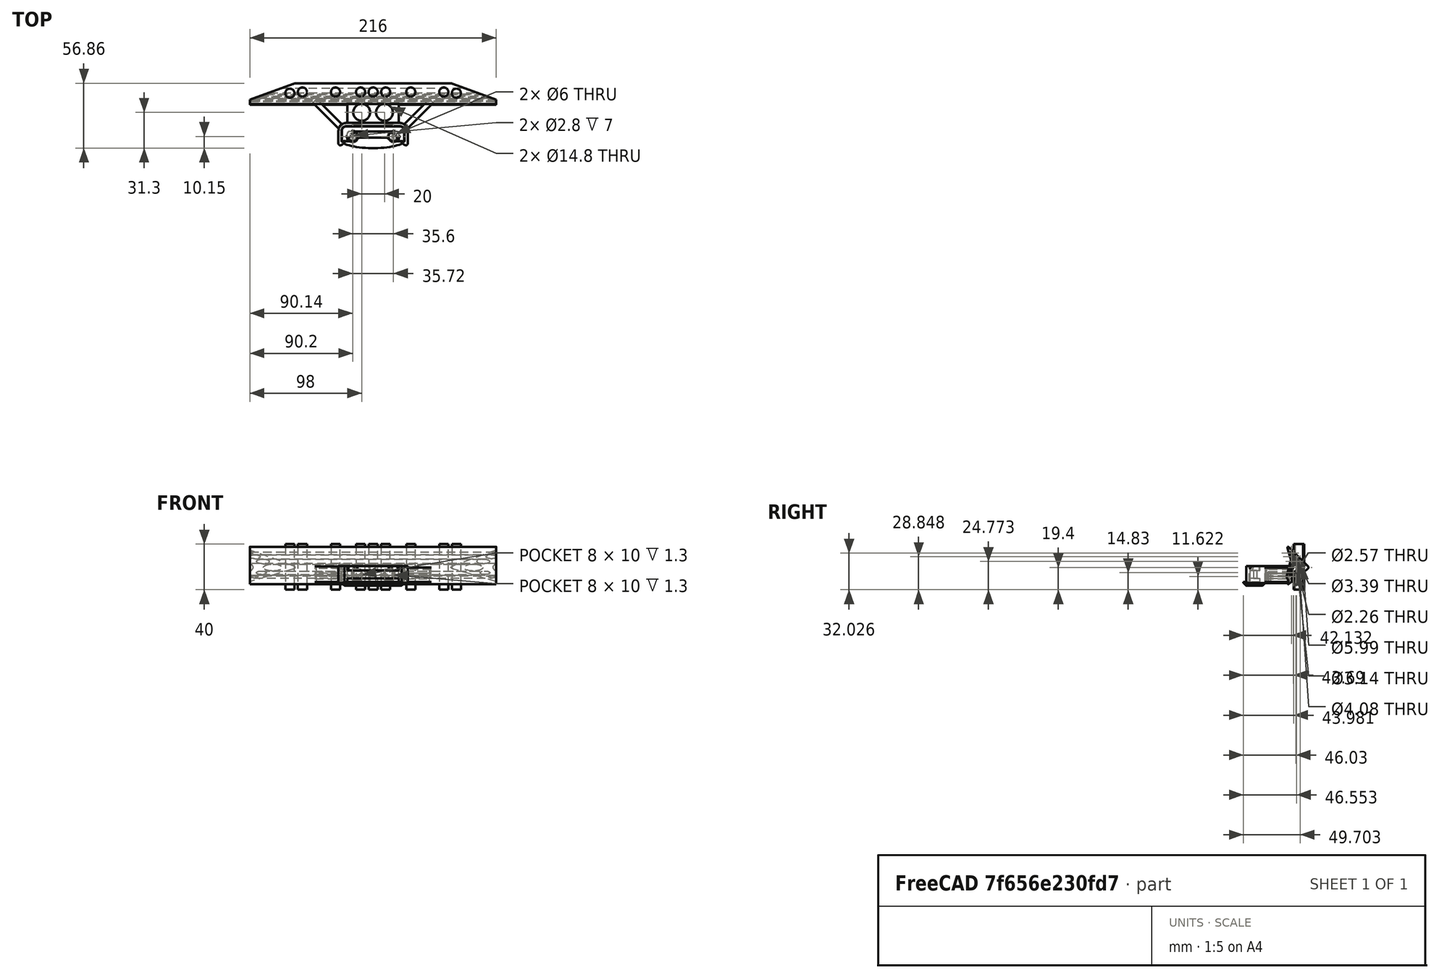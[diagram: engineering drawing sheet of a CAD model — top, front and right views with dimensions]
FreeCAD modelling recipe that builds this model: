
FCSTD DOCUMENT  (FreeCAD 0.21R0.20.1)
Label: 058
License: All rights reserved
LicenseURL: http://en.wikipedia.org/wiki/All_rights_reserved
objects: Part::Cylinder×29, Part::MultiFuse×13, Sketcher::SketchObject×7, Part::Extrusion×7, Part::Box×7, Part::Cut×6, Part::Fillet×5, Part::Chamfer×2
note: 76 computed .brp shape members not serialized (recipe doc carries the construction recipe); baked Part::Feature solids carry a one-line shape summary decoded from their .brp

FEATURE [Sketcher::SketchObject] Sketch  label="attatchmentPiece"
  FullyConstrained = true
  sketch-geometry (20):
    g0: LineSegment StartX=21.05 StartY=0 StartZ=0 EndX=21.05 EndY=-1 EndZ=0
    g1: LineSegment StartX=21.05 StartY=-1 StartZ=0 EndX=21.05 EndY=-4.3 EndZ=0
    g2: LineSegment StartX=-24.15 StartY=4.3 StartZ=0 EndX=21.05 EndY=4.3 EndZ=0
    g3: LineSegment StartX=21.05 StartY=0 StartZ=0 EndX=21.05 EndY=4.3 EndZ=0
    g4-g7: Circle x4 (B-spline internal-alignment scaffolding for g8; pole/knot coordinates omitted)
    g8: BSplineCurve PolesCount=4 KnotsCount=2 Degree=3 IsPeriodic=0
    g9: GeomPoint X=10.05 Y=-1 Z=0
    g10: GeomPoint X=14.55 Y=-4.3 Z=0
    g11: LineSegment StartX=10.05 StartY=-1 StartZ=0 EndX=-10.05 EndY=-1 EndZ=0
    g12: LineSegment StartX=14.55 StartY=-4.3 StartZ=0 EndX=21.05 EndY=-4.3 EndZ=0
    g13: LineSegment StartX=-24.15 StartY=4.3 StartZ=0 EndX=-24.15 EndY=-4.3 EndZ=0
    g14: LineSegment StartX=-13.15 StartY=-1 StartZ=0 EndX=-10.05 EndY=-1 EndZ=0
    g15: LineSegment StartX=-24.15 StartY=-4.3 StartZ=0 EndX=-19.35 EndY=-4.3 EndZ=0
    g16: LineSegment StartX=-19.35 StartY=-4.3 StartZ=0 EndX=-17.65 EndY=-4.3 EndZ=0
    g17: BSplineCurve PolesCount=4 KnotsCount=2 Degree=3 IsPeriodic=0
    g18: Circle CenterX=16.25 CenterY=0 CenterZ=0 NormalX=0 NormalY=0 NormalZ=1 AngleXU=0 Radius=1.4
    g19: Circle CenterX=-19.35 CenterY=0 CenterZ=0 NormalX=0 NormalY=0 NormalZ=1 AngleXU=0 Radius=1.4
  constraints (41):
    c: Vertical(g0)
    c: Coincident(g1,g0)
    c: Vertical(g1)
    c: Block(g0)
    c: Horizontal(g2)
    c: Vertical(g3)
    c: Coincident(g3,g2)
    c: Block(g2)
    c: Block(g3)
    c: Weight(g4) = 1
    c: Equal(g4,g5)
    c: Equal(g4,g6)
    c: Equal(g4,g7)
    c: InternalAlignment(g4-g7 -> g8) x4
    c: InternalAlignment(g9,g8)
    c: InternalAlignment(g10,g8)
    c: Block(g8)
    c: Coincident(g11,g8)
    c: Horizontal(g11)
    c: Coincident(g12,g8)
    c: Coincident(g12,g1)
    c: Horizontal(g12)
    c: Distance(g2) = 45.2
    c: Coincident(g13,g2)
    c: Vertical(g13)
    c: Horizontal(g14)
    c: Distance(g14) = 3.1
    c: Horizontal(g15)
    c: Block(g17)
    c: Coincident(g16,g15)
    c: Coincident(g16,g17)
    c: Horizontal(g16)
    c: Block(g16)
    c: Coincident(g17,g14)
    c: Block(g15)
    c: Block(g11)
    c: Block(g13)
    c: Distance(g15) = 4.8
    c: Distance(g16) = 1.7
    c: Block(g18)
    c: Block(g19)
FEATURE [Part::Extrusion] Extrude  label="attatchmentPiece001"
  Base = -> Sketch
  Dir = (0,0,1)
  DirMode = 2
  FaceMakerClass = Part::FaceMakerBullseye
  LengthFwd = 7
  LengthRev = 0
  Solid = true
  Symmetric = false
FEATURE [Sketcher::SketchObject] Sketch001  label="attatchmentPieceSurround"
  FullyConstrained = true
  sketch-geometry (18):
    g0: LineSegment StartX=25.85 StartY=-4.3 StartZ=0 EndX=21.05 EndY=-4.3 EndZ=0
    g1: LineSegment StartX=25.85 StartY=-4.3 StartZ=0 EndX=25.85 EndY=4.3 EndZ=0
    g2: LineSegment StartX=-21.05 StartY=8.9 StartZ=0 EndX=21.05 EndY=8.9 EndZ=0
    g3: Circle CenterX=21.05 CenterY=8.9 CenterZ=0 NormalX=0 NormalY=0 NormalZ=1 AngleXU=0 Radius=1
    g4: Circle CenterX=25.85 CenterY=8.9 CenterZ=0 NormalX=0 NormalY=0 NormalZ=1 AngleXU=0 Radius=1
    g5: Circle CenterX=25.85 CenterY=4.3 CenterZ=0 NormalX=0 NormalY=0 NormalZ=1 AngleXU=0 Radius=1
    g6: BSplineCurve PolesCount=3 KnotsCount=2 Degree=2 IsPeriodic=0
    g7: GeomPoint X=21.05 Y=8.9 Z=0
    g8: GeomPoint X=25.85 Y=4.3 Z=0
    g9: ArcOfCircle CenterX=19.45 CenterY=2.7 CenterZ=0 NormalX=0 NormalY=0 NormalZ=1 AngleXU=0 Radius=1.6 StartAngle=0 EndAngle=1.5708
    g10: LineSegment StartX=21.05 StartY=2.7 StartZ=0 EndX=21.05 EndY=-4.3 EndZ=0
    g11: BSplineCurve PolesCount=3 KnotsCount=2 Degree=2 IsPeriodic=0
    g12: LineSegment StartX=-28.95 StartY=-4.3 StartZ=0 EndX=-28.95 EndY=4.3 EndZ=0
    g13: LineSegment StartX=-24.15 StartY=-4.3 StartZ=0 EndX=-28.95 EndY=-4.3 EndZ=0
    g14: LineSegment StartX=-24.15 StartY=2.7 StartZ=0 EndX=-24.15 EndY=-4.3 EndZ=0
    g15: ArcOfCircle CenterX=-22.55 CenterY=2.7 CenterZ=0 NormalX=0 NormalY=0 NormalZ=1 AngleXU=0 Radius=1.6 StartAngle=1.5708 EndAngle=3.14159
    g16: LineSegment StartX=-24.15 StartY=8.9 StartZ=0 EndX=-21.05 EndY=8.9 EndZ=0
    g17: LineSegment StartX=-22.55 StartY=4.3 StartZ=0 EndX=19.45 EndY=4.3 EndZ=0
  constraints (38):
    c: Horizontal(g0)
    c: Vertical(g1)
    c: Coincident(g1,g0)
    c: Horizontal(g2)
    c: Distance(g2) = 42.1
    c: Block(g2)
    c: Coincident(g6,g2)
    c: Weight(g3) = 1
    c: Equal(g3,g4)
    c: Equal(g3,g5)
    c: Coincident(g6,g1)
    c: InternalAlignment(g3,g6)
    c: InternalAlignment(g4,g6)
    c: InternalAlignment(g5,g6)
    c: InternalAlignment(g7,g6)
    c: InternalAlignment(g8,g6)
    c: Block(g0)
    c: Block(g6)
    c: Block(g9)
    c: Coincident(g10,g9)
    c: Coincident(g10,g0)
    c: Vertical(g10)
    c: Horizontal(g13)
    c: Coincident(g12,g13)
    c: Vertical(g12)
    c: Coincident(g11,g12)
    c: Block(g12)
    c: Block(g11)
    c: Block(g15)
    c: Coincident(g14,g15)
    c: Coincident(g14,g13)
    c: Vertical(g14)
    c: Coincident(g16,g11)
    c: Coincident(g16,g2)
    c: Horizontal(g16)
    c: Coincident(g17,g15)
    c: Coincident(g17,g9)
    c: Horizontal(g17)
FEATURE [Part::Extrusion] Extrude001  label="attatchmentPieceSurround001"
  Base = -> Sketch001
  Dir = (0,0,1)
  DirMode = 2
  FaceMakerClass = Part::FaceMakerBullseye
  LengthFwd = 14.7
  LengthRev = 0
  Placement = pos=(0,0,-4.1) rot=(0,0,1;0rad)
  Solid = true
  Symmetric = false
FEATURE [Sketcher::SketchObject] Sketch002  label="attatchmentPieceEndScrewHoleCaps"
  FullyConstrained = true
  sketch-geometry (10):
    g0: ArcOfCircle CenterX=16.25 CenterY=0 CenterZ=0 NormalX=0 NormalY=0 NormalZ=1 AngleXU=0 Radius=4.3 StartAngle=2.05456 EndAngle=5.79942
    g1: LineSegment StartX=14.25 StartY=3.80657 StartZ=0 EndX=14.25 EndY=6 EndZ=0
    g2: LineSegment StartX=20.0566 StartY=-2 StartZ=0 EndX=22.25 EndY=-2 EndZ=0
    g3: LineSegment StartX=22.25 StartY=-2 StartZ=0 EndX=22.25 EndY=6 EndZ=0
    g4: LineSegment StartX=14.25 StartY=6 StartZ=0 EndX=22.25 EndY=6 EndZ=0
    g5: LineSegment StartX=-25.35 StartY=-2 StartZ=0 EndX=-25.35 EndY=6 EndZ=0
    g6: LineSegment StartX=-25.35 StartY=-2 StartZ=0 EndX=-23.1566 EndY=-2 EndZ=0
    g7: LineSegment StartX=-17.35 StartY=6 StartZ=0 EndX=-25.35 EndY=6 EndZ=0
    g8: LineSegment StartX=-17.35 StartY=3.80657 StartZ=0 EndX=-17.35 EndY=6 EndZ=0
    g9: ArcOfCircle CenterX=-19.35 CenterY=0 CenterZ=0 NormalX=0 NormalY=0 NormalZ=1 AngleXU=0 Radius=4.3 StartAngle=3.62536 EndAngle=7.37022
  constraints (25):
    c: Block(g0)
    c: Vertical(g1)
    c: Horizontal(g2)
    c: Coincident(g3,g2)
    c: Vertical(g3)
    c: Coincident(g4,g1)
    c: Horizontal(g4)
    c: Coincident(g3,g4)
    c: Block(g4)
    c: Block(g3)
    c: Coincident(g0,g1)
    c: Coincident(g0,g2)
    c: Block(g1)
    c: Block(g9)
    c: Horizontal(g6)
    c: Vertical(g8)
    c: Coincident(g7,g8)
    c: Horizontal(g7)
    c: Coincident(g5,g6)
    c: Vertical(g5)
    c: Coincident(g5,g7)
    c: Block(g7)
    c: Block(g5)
    c: Coincident(g9,g6)
    c: Coincident(g9,g8)
FEATURE [Part::Extrusion] Extrude002  label="attatchmentPieceEndScrewHoleCaps001"
  Base = -> Sketch002
  Dir = (0,0,1)
  DirMode = 2
  FaceMakerClass = Part::FaceMakerBullseye
  LengthFwd = 3.6
  LengthRev = 0
  Placement = pos=(0,0,7) rot=(0,0,1;0rad)
  Solid = true
  Symmetric = false
FEATURE [Sketcher::SketchObject] Sketch003  label="mainBumpperPieceAttatchment"
  FullyConstrained = true
  sketch-geometry (42):
    g0: Circle CenterX=28.85 CenterY=4.3 CenterZ=0 NormalX=0 NormalY=0 NormalZ=1 AngleXU=0 Radius=1
    g1: Circle CenterX=28.85 CenterY=11.9 CenterZ=0 NormalX=0 NormalY=0 NormalZ=1 AngleXU=0 Radius=1
    g2: Circle CenterX=21.05 CenterY=11.9 CenterZ=0 NormalX=0 NormalY=0 NormalZ=1 AngleXU=0 Radius=1
    g3: BSplineCurve PolesCount=3 KnotsCount=2 Degree=2 IsPeriodic=0
    g4: GeomPoint X=28.85 Y=4.3 Z=0
    g5: GeomPoint X=21.05 Y=11.9 Z=0
    g6: LineSegment StartX=-21.05 StartY=11.9 StartZ=0 EndX=21.05 EndY=11.9 EndZ=0
    g7: LineSegment StartX=28.85 StartY=4.3 StartZ=0 EndX=28.85 EndY=-4.3 EndZ=0
    g8: Circle CenterX=21.05 CenterY=9.2 CenterZ=0 NormalX=0 NormalY=0 NormalZ=1 AngleXU=0 Radius=1
    g9: Circle CenterX=26.15 CenterY=9.2 CenterZ=0 NormalX=0 NormalY=0 NormalZ=1 AngleXU=0 Radius=1
    g10: Circle CenterX=26.15 CenterY=4.3 CenterZ=0 NormalX=0 NormalY=0 NormalZ=1 AngleXU=0 Radius=1
    g11: BSplineCurve PolesCount=3 KnotsCount=2 Degree=2 IsPeriodic=0
    g12: GeomPoint X=21.05 Y=9.2 Z=0
    g13: GeomPoint X=26.15 Y=4.3 Z=0
    g14: LineSegment StartX=-21.05 StartY=9.2 StartZ=0 EndX=21.05 EndY=9.2 EndZ=0
    g15: LineSegment StartX=26.15 StartY=-4.3 StartZ=0 EndX=26.15 EndY=4.3 EndZ=0
    g16: LineSegment StartX=26.15 StartY=-4.3 StartZ=0 EndX=26.15 EndY=-4.6 EndZ=0
    g17: LineSegment StartX=23.45 StartY=-4.6 StartZ=0 EndX=26.15 EndY=-4.6 EndZ=0
    g18: LineSegment StartX=28.85 StartY=-4.3 StartZ=0 EndX=28.85 EndY=-7.9 EndZ=0
    g19: LineSegment StartX=23.45 StartY=-4.6 StartZ=0 EndX=23.45 EndY=-5.3 EndZ=0
    g20: Circle CenterX=28.85 CenterY=-7.9 CenterZ=0 NormalX=0 NormalY=0 NormalZ=1 AngleXU=0 Radius=1
    g21: Circle CenterX=26.15 CenterY=-8.2 CenterZ=0 NormalX=0 NormalY=0 NormalZ=1 AngleXU=0 Radius=1
    g22: Circle CenterX=23.45 CenterY=-5.3 CenterZ=0 NormalX=0 NormalY=0 NormalZ=1 AngleXU=0 Radius=1
    g23: BSplineCurve PolesCount=3 KnotsCount=2 Degree=2 IsPeriodic=0
    g24: GeomPoint X=28.85 Y=-7.9 Z=0
    g25: GeomPoint X=23.45 Y=-5.3 Z=0
    g26: LineSegment StartX=-21.05 StartY=9.2 StartZ=0 EndX=-24.15 EndY=9.2 EndZ=0
    g27: BSplineCurve PolesCount=3 KnotsCount=2 Degree=2 IsPeriodic=0
    g28: LineSegment StartX=-29.25 StartY=-4.3 StartZ=0 EndX=-29.25 EndY=-4.6 EndZ=0
    g29: LineSegment StartX=-29.25 StartY=-4.6 StartZ=0 EndX=-26.55 EndY=-4.6 EndZ=0
    g30: LineSegment StartX=-31.95 StartY=-4.3 StartZ=0 EndX=-31.95 EndY=-7.9 EndZ=0
    g31: LineSegment StartX=-26.55 StartY=-4.6 StartZ=0 EndX=-26.55 EndY=-5.3 EndZ=0
    g32: Circle CenterX=-31.95 CenterY=-7.9 CenterZ=0 NormalX=0 NormalY=0 NormalZ=1 AngleXU=0 Radius=1
    g33: Circle CenterX=-29.25 CenterY=-8.2 CenterZ=0 NormalX=0 NormalY=0 NormalZ=1 AngleXU=0 Radius=1
    g34: Circle CenterX=-26.55 CenterY=-5.3 CenterZ=0 NormalX=0 NormalY=0 NormalZ=1 AngleXU=0 Radius=1
    g35: BSplineCurve PolesCount=3 KnotsCount=2 Degree=2 IsPeriodic=0
    g36: GeomPoint X=-31.95 Y=-7.9 Z=0
    g37: GeomPoint X=-26.55 Y=-5.3 Z=0
    g38: LineSegment StartX=-31.95 StartY=4.3 StartZ=0 EndX=-31.95 EndY=-4.3 EndZ=0
    g39: LineSegment StartX=-29.25 StartY=-4.3 StartZ=0 EndX=-29.25 EndY=4.3 EndZ=0
    g40: BSplineCurve PolesCount=3 KnotsCount=2 Degree=2 IsPeriodic=0
    g41: LineSegment StartX=-21.05 StartY=11.9 StartZ=0 EndX=-24.15 EndY=11.9 EndZ=0
  constraints (78):
    c: Weight(g0) = 1
    c: Equal(g0,g1)
    c: Equal(g0,g2)
    c: InternalAlignment(g0,g3)
    c: InternalAlignment(g1,g3)
    c: InternalAlignment(g2,g3)
    c: InternalAlignment(g4,g3)
    c: InternalAlignment(g5,g3)
    c: Block(g3)
    c: Horizontal(g6)
    c: Vertical(g7)
    c: Block(g7)
    c: Block(g6)
    c: Weight(g8) = 1
    c: Equal(g8,g9)
    c: Equal(g8,g10)
    c: InternalAlignment(g8,g11)
    c: InternalAlignment(g9,g11)
    c: InternalAlignment(g10,g11)
    c: InternalAlignment(g12,g11)
    c: InternalAlignment(g13,g11)
    c: Horizontal(g14)
    c: Vertical(g15)
    c: Block(g11)
    c: Block(g15)
    c: Block(g14)
    c: Coincident(g16,g15)
    c: Vertical(g16)
    c: Distance(g16) = 0.3
    c: Horizontal(g17)
    c: Coincident(g17,g16)
    c: Coincident(g18,g7)
    c: Vertical(g18)
    c: Distance(g18) = 3.6
    c: Vertical(g19)
    c: Coincident(g19,g17)
    c: Coincident(g23,g18)
    c: Weight(g20) = 1
    c: Equal(g20,g21)
    c: Equal(g20,g22)
    c: Coincident(g23,g19)
    c: InternalAlignment(g20,g23)
    c: InternalAlignment(g21,g23)
    c: InternalAlignment(g22,g23)
    c: InternalAlignment(g24,g23)
    c: InternalAlignment(g25,g23)
    c: Block(g23)
    c: Horizontal(g26)
    c: Distance(g26) = 3.1
    c: Block(g27)
    c: Vertical(g38)
    c: Block(g38)
    c: Vertical(g39)
    c: Block(g40)
    c: Block(g39)
    c: Vertical(g28)
    c: Coincident(g28,g39)
    c: Coincident(g29,g28)
    c: Horizontal(g29)
    c: Vertical(g30)
    c: Coincident(g30,g38)
    c: Coincident(g31,g29)
    c: Vertical(g31)
    c: Coincident(g35,g30)
    c: Equal(g32,g33)
    c: Equal(g32,g34)
    c: Coincident(g35,g31)
    c: InternalAlignment(g32,g35)
    c: InternalAlignment(g33,g35)
    c: InternalAlignment(g34,g35)
    c: InternalAlignment(g36,g35)
    c: InternalAlignment(g37,g35)
    c: Block(g35)
    c: Coincident(g40,g26)
    c: Block(g29)
    c: Horizontal(g41)
    c: Equal(g26,g41) = 3.1
    c: Coincident(g41,g6)
FEATURE [Part::Box] Box  label="bumpperExtension"
  AttacherType = Attacher::AttachEngine3D
  Height = 14.7
  Length = 45.2
  Placement = pos=(-24.15,11.9,-4.1) rot=(0,0,1;0rad)
  Width = 18
FEATURE [Sketcher::SketchObject] Sketch004  label="bumpperMain"
  FullyConstrained = true
  Placement = pos=(0,0,0) rot=(0.57735,0.57735,0.57735;2.0944rad)
  sketch-geometry (62):
    g0: Circle CenterX=-3.12329 CenterY=2.49901 CenterZ=0 NormalX=0 NormalY=0 NormalZ=1 AngleXU=0 Radius=1
    g1: Circle CenterX=0 CenterY=0 CenterZ=0 NormalX=0 NormalY=0 NormalZ=1 AngleXU=0 Radius=1
    g2: Circle CenterX=-1.35243 CenterY=3.60648 CenterZ=0 NormalX=0 NormalY=0 NormalZ=1 AngleXU=0 Radius=1
    g3: BSplineCurve PolesCount=3 KnotsCount=2 Degree=2 IsPeriodic=0
    g4: GeomPoint X=-3.12329 Y=2.49901 Z=0
    g5: GeomPoint X=-1.35243 Y=3.60648 Z=0
    g6: Circle CenterX=-2.83953 CenterY=33.0261 CenterZ=0 NormalX=0 NormalY=0 NormalZ=1 AngleXU=0 Radius=1
    g7: Circle CenterX=0 CenterY=35.8434 CenterZ=0 NormalX=0 NormalY=0 NormalZ=1 AngleXU=0 Radius=1
    g8: Circle CenterX=-1.15771 CenterY=32.0146 CenterZ=0 NormalX=0 NormalY=0 NormalZ=1 AngleXU=0 Radius=1
    g9: BSplineCurve PolesCount=3 KnotsCount=2 Degree=2 IsPeriodic=0
    g10: GeomPoint X=-2.83953 Y=33.0261 Z=0
    g11: GeomPoint X=-1.15771 Y=32.0146 Z=0
    g12: Circle CenterX=-18.2963 CenterY=17.6904 CenterZ=0 NormalX=0 NormalY=0 NormalZ=1 AngleXU=0 Radius=1
    g13: Circle CenterX=-20 CenterY=16 CenterZ=0 NormalX=0 NormalY=0 NormalZ=1 AngleXU=0 Radius=1
    g14: Circle CenterX=-18.1259 CenterY=14.5008 CenterZ=0 NormalX=0 NormalY=0 NormalZ=1 AngleXU=0 Radius=1
    g15: BSplineCurve PolesCount=3 KnotsCount=2 Degree=2 IsPeriodic=0
    g16: GeomPoint X=-18.2963 Y=17.6904 Z=0
    g17: GeomPoint X=-18.1259 Y=14.5008 Z=0
    g18: LineSegment StartX=-18.2963 StartY=17.6904 StartZ=0 EndX=-2.83953 EndY=33.0261 EndZ=0
    g19: LineSegment StartX=-18.1259 StartY=14.5008 StartZ=0 EndX=-3.12329 EndY=2.49901 EndZ=0
    g20: Circle CenterX=-11.9527 CenterY=16 CenterZ=0 NormalX=0 NormalY=0 NormalZ=1 AngleXU=0 Radius=2.99582
    g21: Circle CenterX=-8.803 CenterY=21.3731 CenterZ=0 NormalX=0 NormalY=0 NormalZ=1 AngleXU=0 Radius=2.03939
    g22: Circle CenterX=-6.23123 CenterY=25.4475 CenterZ=0 NormalX=0 NormalY=0 NormalZ=1 AngleXU=0 Radius=1.69309
    g23: Circle CenterX=-4.38186 CenterY=28.6261 CenterZ=0 NormalX=0 NormalY=0 NormalZ=1 AngleXU=0 Radius=1.13029
    g24: Circle CenterX=-8.28033 CenterY=11.4296 CenterZ=0 NormalX=0 NormalY=0 NormalZ=1 AngleXU=0 Radius=1.57213
    g25: Circle CenterX=-5.93972 CenterY=8.22213 CenterZ=0 NormalX=0 NormalY=0 NormalZ=1 AngleXU=0 Radius=1.28743
    g26: Circle CenterX=-3.47023 CenterY=24.3665 CenterZ=0 NormalX=0 NormalY=0 NormalZ=1 AngleXU=0 Radius=1
    g27: Circle CenterX=-3.90437 CenterY=22.9307 CenterZ=0 NormalX=0 NormalY=0 NormalZ=1 AngleXU=0 Radius=1
    g28: Circle CenterX=-3.53772 CenterY=21.4762 CenterZ=0 NormalX=0 NormalY=0 NormalZ=1 AngleXU=0 Radius=1
    g29: BSplineCurve PolesCount=3 KnotsCount=2 Degree=2 IsPeriodic=0
    g30: GeomPoint X=-3.47023 Y=24.3665 Z=0
    g31: GeomPoint X=-3.53772 Y=21.4762 Z=0
    g32: LineSegment StartX=-1.15771 StartY=32.0146 StartZ=0 EndX=-3.47023 EndY=24.3665 EndZ=0
    g33: Circle CenterX=-5.41867 CenterY=17.9226 CenterZ=0 NormalX=0 NormalY=0 NormalZ=1 AngleXU=0 Radius=1
    g34: Circle CenterX=-6 CenterY=16 CenterZ=0 NormalX=0 NormalY=0 NormalZ=1 AngleXU=0 Radius=1
    g35: Circle CenterX=-5.22753 CenterY=13.9401 CenterZ=0 NormalX=0 NormalY=0 NormalZ=1 AngleXU=0 Radius=1
    g36: BSplineCurve PolesCount=3 KnotsCount=2 Degree=2 IsPeriodic=0
    g37: GeomPoint X=-5.41867 Y=17.9226 Z=0
    g38: GeomPoint X=-5.22753 Y=13.9401 Z=0
    g39: Circle CenterX=-3.98946 CenterY=10.6386 CenterZ=0 NormalX=0 NormalY=0 NormalZ=1 AngleXU=0 Radius=1
    g40: Circle CenterX=-2.58497 CenterY=6.89324 CenterZ=0 NormalX=0 NormalY=0 NormalZ=1 AngleXU=0 Radius=1
    g41: Circle CenterX=-3.11001 CenterY=10.8586 CenterZ=0 NormalX=0 NormalY=0 NormalZ=1 AngleXU=0 Radius=1
    g42: BSplineCurve PolesCount=3 KnotsCount=2 Degree=2 IsPeriodic=0
    g43: GeomPoint X=-3.98946 Y=10.6386 Z=0
    g44: GeomPoint X=-3.11001 Y=10.8586 Z=0
    g45: Circle CenterX=-1.35243 CenterY=3.60648 CenterZ=0 NormalX=0 NormalY=0 NormalZ=1 AngleXU=0 Radius=1
    g46: Circle CenterX=-1.76142 CenterY=4.69712 CenterZ=0 NormalX=0 NormalY=0 NormalZ=1 AngleXU=0 Radius=1
    g47: Circle CenterX=-1.05937 CenterY=5.79125 CenterZ=0 NormalX=0 NormalY=0 NormalZ=1 AngleXU=0 Radius=1
    g48: BSplineCurve PolesCount=3 KnotsCount=2 Degree=2 IsPeriodic=0
    g49: GeomPoint X=-1.35243 Y=3.60648 Z=0
    g50: GeomPoint X=-1.05937 Y=5.79125 Z=0
    g51: Circle CenterX=-0.519336 CenterY=6.6329 CenterZ=0 NormalX=0 NormalY=0 NormalZ=1 AngleXU=0 Radius=1
    g52: Circle CenterX=0 CenterY=7.44228 CenterZ=0 NormalX=0 NormalY=0 NormalZ=1 AngleXU=0 Radius=1
    g53: Circle CenterX=-0.244436 CenterY=8.41194 CenterZ=0 NormalX=0 NormalY=0 NormalZ=1 AngleXU=0 Radius=1
    g54: BSplineCurve PolesCount=3 KnotsCount=2 Degree=2 IsPeriodic=0
    g55: GeomPoint X=-0.519336 Y=6.6329 Z=0
    g56: GeomPoint X=-0.244436 Y=8.41194 Z=0
    g57: LineSegment StartX=-3.53772 StartY=21.4762 StartZ=0 EndX=-0.244436 EndY=8.41194 EndZ=0
    g58: LineSegment StartX=-5.22753 StartY=13.9401 StartZ=0 EndX=-3.98946 EndY=10.6386 EndZ=0
    g59: LineSegment StartX=-1.05937 StartY=5.79125 StartZ=0 EndX=-0.519336 EndY=6.6329 EndZ=0
    g60: BSplineCurve PolesCount=3 KnotsCount=2 Degree=2 IsPeriodic=0
    g61: LineSegment StartX=-4.0304 StartY=17.8099 StartZ=0 EndX=-3.11001 EndY=10.8586 EndZ=0
  constraints (96):
    c: Weight(g0) = 1
    c: Equal(g0,g1)
    c: Equal(g0,g2)
    c: InternalAlignment(g0,g3)
    c: InternalAlignment(g1,g3)
    c: InternalAlignment(g2,g3)
    c: InternalAlignment(g4,g3)
    c: InternalAlignment(g5,g3)
    c: Block(g3)
    c: Weight(g6) = 1
    c: Equal(g6,g7)
    c: Equal(g6,g8)
    c: InternalAlignment(g6,g9)
    c: InternalAlignment(g7,g9)
    c: InternalAlignment(g8,g9)
    c: InternalAlignment(g10,g9)
    c: InternalAlignment(g11,g9)
    c: Block(g9)
    c: Weight(g12) = 1
    c: Equal(g12,g13)
    c: Equal(g12,g14)
    c: InternalAlignment(g12,g15)
    c: InternalAlignment(g13,g15)
    c: InternalAlignment(g14,g15)
    c: InternalAlignment(g16,g15)
    c: InternalAlignment(g17,g15)
    c: Block(g15)
    c: Coincident(g18,g15)
    c: Coincident(g18,g9)
    c: Coincident(g19,g15)
    c: Coincident(g19,g3)
    c: Block(g25)
    c: Block(g24)
    c: Block(g20)
    c: Block(g21)
    c: Block(g22)
    c: Block(g23)
    c: Weight(g26) = 1
    c: Equal(g26,g27)
    c: Equal(g26,g28)
    c: InternalAlignment(g26,g29)
    c: InternalAlignment(g27,g29)
    c: InternalAlignment(g28,g29)
    c: InternalAlignment(g30,g29)
    c: InternalAlignment(g31,g29)
    c: Block(g29)
    c: Coincident(g32,g9)
    c: Coincident(g32,g29)
    c: Weight(g33) = 1
    c: Equal(g33,g34)
    c: Equal(g33,g35)
    c: InternalAlignment(g33,g36)
    c: InternalAlignment(g34,g36)
    c: InternalAlignment(g35,g36)
    c: InternalAlignment(g37,g36)
    c: InternalAlignment(g38,g36)
    c: Block(g36)
    c: Weight(g39) = 1
    c: Equal(g39,g40)
    c: Equal(g39,g41)
    c: InternalAlignment(g39,g42)
    c: InternalAlignment(g40,g42)
    c: InternalAlignment(g41,g42)
    c: InternalAlignment(g43,g42)
    c: InternalAlignment(g44,g42)
    c: Block(g42)
    c: Coincident(g48,g3)
    c: Weight(g45) = 1
    c: Equal(g45,g46)
    c: Equal(g45,g47)
    c: InternalAlignment(g45,g48)
    c: InternalAlignment(g46,g48)
    c: InternalAlignment(g47,g48)
    c: InternalAlignment(g49,g48)
    c: InternalAlignment(g50,g48)
    c: Block(g48)
    c: Weight(g51) = 1
    c: Equal(g51,g52)
    c: Equal(g51,g53)
    c: InternalAlignment(g51,g54)
    c: InternalAlignment(g52,g54)
    c: InternalAlignment(g53,g54)
    c: InternalAlignment(g55,g54)
    c: InternalAlignment(g56,g54)
    c: Block(g54)
    c: Coincident(g57,g29)
    c: Coincident(g57,g54)
    c: Block(g57)
    c: Coincident(g58,g36)
    c: Coincident(g58,g42)
    c: Coincident(g59,g48)
    c: Coincident(g59,g54)
    c: Block(g60)
    c: Coincident(g60,g36)
    c: Coincident(g61,g60)
    c: Coincident(g61,g42)
FEATURE [Part::Extrusion] Extrude004  label="bumpperMain001"
  Base = -> Sketch004
  Dir = (1,0,0)
  DirMode = 2
  FaceMakerClass = Part::FaceMakerBullseye
  LengthFwd = 216
  LengthRev = 0
  Placement = pos=(106.45,27.6,-6.6) rot=(0,0,1;3.14159rad)
  Solid = true
  Symmetric = false
FEATURE [Sketcher::SketchObject] Sketch005  label="attatchmentPieceBottom"
  FullyConstrained = true
  sketch-geometry (20):
    g0: LineSegment StartX=25.85 StartY=-4.3 StartZ=0 EndX=25.85 EndY=4.3 EndZ=0
    g1: LineSegment StartX=-21.05 StartY=8.9 StartZ=0 EndX=21.05 EndY=8.9 EndZ=0
    g2: Circle CenterX=21.05 CenterY=8.9 CenterZ=0 NormalX=0 NormalY=0 NormalZ=1 AngleXU=0 Radius=1
    g3: Circle CenterX=25.85 CenterY=8.9 CenterZ=0 NormalX=0 NormalY=0 NormalZ=1 AngleXU=0 Radius=1
    g4: Circle CenterX=25.85 CenterY=4.3 CenterZ=0 NormalX=0 NormalY=0 NormalZ=1 AngleXU=0 Radius=1
    g5: BSplineCurve PolesCount=3 KnotsCount=2 Degree=2 IsPeriodic=0
    g6: GeomPoint X=21.05 Y=8.9 Z=0
    g7: GeomPoint X=25.85 Y=4.3 Z=0
    g8: BSplineCurve PolesCount=3 KnotsCount=2 Degree=2 IsPeriodic=0
    g9: LineSegment StartX=-28.95 StartY=-4.3 StartZ=0 EndX=-28.95 EndY=4.3 EndZ=0
    g10: LineSegment StartX=-24.15 StartY=8.9 StartZ=0 EndX=-21.05 EndY=8.9 EndZ=0
    g11: Circle CenterX=-19.41 CenterY=0 CenterZ=0 NormalX=0 NormalY=0 NormalZ=1 AngleXU=0 Radius=3
    g12: Circle CenterX=16.3103 CenterY=0 CenterZ=0 NormalX=0 NormalY=0 NormalZ=1 AngleXU=0 Radius=3
    g13-g16: Circle x4 (B-spline internal-alignment scaffolding for g17; pole/knot coordinates omitted)
    g17: BSplineCurve PolesCount=4 KnotsCount=2 Degree=3 IsPeriodic=0
    g18: GeomPoint X=-28.95 Y=-4.3 Z=0
    g19: GeomPoint X=25.85 Y=-4.3 Z=0
  constraints (36):
    c: Vertical(g0)
    c: Horizontal(g1)
    c: Distance(g1) = 42.1
    c: Block(g1)
    c: Coincident(g5,g1)
    c: Weight(g2) = 1
    c: Equal(g2,g3)
    c: Equal(g2,g4)
    c: Coincident(g5,g0)
    c: InternalAlignment(g2,g5)
    c: InternalAlignment(g3,g5)
    c: InternalAlignment(g4,g5)
    c: InternalAlignment(g6,g5)
    c: InternalAlignment(g7,g5)
    c: Block(g5)
    c: Vertical(g9)
    c: Coincident(g8,g9)
    c: Block(g9)
    c: Block(g8)
    c: Coincident(g10,g8)
    c: Coincident(g10,g1)
    c: Horizontal(g10)
    c: PointOnObject(g12,g-1)
    c: PointOnObject(g11,g-1)
    c: Block(g11)
    c: Block(g12)
    c: Coincident(g17,g9)
    c: Weight(g13) = 1
    c: Equal(g13,g14)
    c: Equal(g13,g15)
    c: Equal(g13,g16)
    c: Coincident(g17,g0)
    c: InternalAlignment(g13-g16 -> g17) x4
    c: InternalAlignment(g18,g17)
    c: InternalAlignment(g19,g17)
    c: Block(g17)
FEATURE [Part::Extrusion] Extrude005  label="removeFromMainBumpperPieceAttatchment"
  Base = -> Sketch005
  Dir = (0,0,1)
  DirMode = 2
  FaceMakerClass = Part::FaceMakerBullseye
  LengthFwd = 3.2
  LengthRev = 0
  Placement = pos=(0,0,-6.2) rot=(0,0,1;0rad)
  Solid = true
  Symmetric = false
FEATURE [Part::Extrusion] Extrude006  label="mainBumpperPieceAttatchment001"
  Base = -> Sketch003
  Dir = (0,0,1)
  DirMode = 2
  FaceMakerClass = Part::FaceMakerBullseye
  LengthFwd = 14.7
  LengthRev = 0
  Placement = pos=(0,0,-4.1) rot=(0,0,1;0rad)
  Solid = true
  Symmetric = false
FEATURE [Part::Cylinder] Cylinder  label="removeFromBumpperExtension"
  Angle = 360
  AttacherType = Attacher::AttachEngine3D
  FirstAngle = 0
  Height = 20
  Placement = pos=(8.45,21.15,-8) rot=(0,0,1;0rad)
  Radius = 7.4
  SecondAngle = 0
FEATURE [Part::Cylinder] Cylinder001  label="removeFromBumpperExtension001"
  Angle = 360
  AttacherType = Attacher::AttachEngine3D
  FirstAngle = 0
  Height = 20
  Placement = pos=(-11.55,21.15,-8) rot=(0,0,1;0rad)
  Radius = 7.4
  SecondAngle = 0
FEATURE [Part::MultiFuse] Fusion  label="removeFromBumpperExtension002"
  Shapes = -> [Cylinder,Cylinder001]
FEATURE [Part::Cylinder] Cylinder002  label="removeFromBumpperExtension004"
  Angle = 360
  AttacherType = Attacher::AttachEngine3D
  FirstAngle = 0
  Height = 20
  Placement = pos=(8.45,21.15,-8) rot=(0,0,1;0rad)
  Radius = 7.4
  SecondAngle = 0
FEATURE [Part::Cylinder] Cylinder003  label="removeFromBumpperExtension005"
  Angle = 360
  AttacherType = Attacher::AttachEngine3D
  FirstAngle = 0
  Height = 20
  Placement = pos=(-11.55,21.15,-8) rot=(0,0,1;0rad)
  Radius = 7.4
  SecondAngle = 0
FEATURE [Part::MultiFuse] Fusion001  label="removeFromBumpperMain"
  Shapes = -> [Cylinder002,Cylinder003]
FEATURE [Part::Cut] Cut  label="bumpperExtension001"
  Base = -> Box
  Tool = -> Fusion
FEATURE [Part::Fillet] Fillet  label="bumpperExtension002"
  Base = -> Cut
  Edges = 4 edges r=3: [Edge2,Edge4,Edge9,Edge14]
FEATURE [Part::Box] Box001  label="bumpperExtensionBumpHole"
  AttacherType = Attacher::AttachEngine3D
  Height = 10
  Length = 8
  Placement = pos=(8.45,9.2,-1.8) rot=(0,0,1;0rad)
  Width = 1.3
FEATURE [Part::Box] Box002  label="bumpperExtensionBumpHole001"
  AttacherType = Attacher::AttachEngine3D
  Height = 10
  Length = 8
  Placement = pos=(-19.55,9.2,-1.8) rot=(0,0,1;0rad)
  Width = 1.3
FEATURE [Part::Box] Box003  label="attatchmentPieceSurroundBump"
  AttacherType = Attacher::AttachEngine3D
  Height = 9.2
  Length = 7.2
  Placement = pos=(8.85,8.9,-1.4) rot=(0,0,1;0rad)
  Width = 1.3
FEATURE [Part::Box] Box004  label="attatchmentPieceSurroundBump001"
  AttacherType = Attacher::AttachEngine3D
  Height = 9.2
  Length = 7.2
  Placement = pos=(-19.15,8.9,-1.4) rot=(0,0,1;0rad)
  Width = 1.3
FEATURE [Part::MultiFuse] Fusion002  label="attatchmentPieceSurroundBump002"
  Placement = pos=(0,-0.4,0) rot=(0,0,1;0rad)
  Shapes = -> [Box004,Box003]
FEATURE [Part::MultiFuse] Fusion003  label="bumpperExtensionBumpHole002"
  Shapes = -> [Box002,Box001]
FEATURE [Part::Cut] Cut002  label="mainBumpperPieceAttatchment002"
  Base = -> Extrude006
  Tool = -> Fusion003
FEATURE [Part::Fillet] Fillet003  label="attatchmentPieceEndScrewHoleCaps002"
  Base = -> Extrude002
  Edges = 6 edges r=2.4: [Edge4,Edge7,Edge15,Edge25,Edge28,Edge30]
FEATURE [Part::Fillet] Fillet004  label="attatchmentPieceSurround002"
  Base = -> Extrude001
  Edges = 3 edges r=1.2: [Edge19,Edge25,Edge31]
FEATURE [Part::Fillet] Fillet006  label="mainBumpperPieceAttatchment003"
  Base = -> Cut002
  Edges = 2 edges r=1.6: [Edge2,Edge55]
FEATURE [Sketcher::SketchObject] Sketch006  label="attatchmentPieceBottom002"
  FullyConstrained = true
  sketch-geometry (20):
    g0: LineSegment StartX=25.85 StartY=-4.3 StartZ=0 EndX=25.85 EndY=4.3 EndZ=0
    g1: LineSegment StartX=-21.05 StartY=8.9 StartZ=0 EndX=21.05 EndY=8.9 EndZ=0
    g2: Circle CenterX=21.05 CenterY=8.9 CenterZ=0 NormalX=0 NormalY=0 NormalZ=1 AngleXU=0 Radius=1
    g3: Circle CenterX=25.85 CenterY=8.9 CenterZ=0 NormalX=0 NormalY=0 NormalZ=1 AngleXU=0 Radius=1
    g4: Circle CenterX=25.85 CenterY=4.3 CenterZ=0 NormalX=0 NormalY=0 NormalZ=1 AngleXU=0 Radius=1
    g5: BSplineCurve PolesCount=3 KnotsCount=2 Degree=2 IsPeriodic=0
    g6: GeomPoint X=21.05 Y=8.9 Z=0
    g7: GeomPoint X=25.85 Y=4.3 Z=0
    g8: BSplineCurve PolesCount=3 KnotsCount=2 Degree=2 IsPeriodic=0
    g9: LineSegment StartX=-28.95 StartY=-4.3 StartZ=0 EndX=-28.95 EndY=4.3 EndZ=0
    g10: LineSegment StartX=-24.15 StartY=8.9 StartZ=0 EndX=-21.05 EndY=8.9 EndZ=0
    g11: Circle CenterX=-19.41 CenterY=0 CenterZ=0 NormalX=0 NormalY=0 NormalZ=1 AngleXU=0 Radius=3
    g12: Circle CenterX=16.3103 CenterY=0 CenterZ=0 NormalX=0 NormalY=0 NormalZ=1 AngleXU=0 Radius=3
    g13-g16: Circle x4 (B-spline internal-alignment scaffolding for g17; pole/knot coordinates omitted)
    g17: BSplineCurve PolesCount=4 KnotsCount=2 Degree=3 IsPeriodic=0
    g18: GeomPoint X=-28.95 Y=-4.3 Z=0
    g19: GeomPoint X=25.85 Y=-4.3 Z=0
  constraints (36):
    c: Vertical(g0)
    c: Horizontal(g1)
    c: Distance(g1) = 42.1
    c: Block(g1)
    c: Coincident(g5,g1)
    c: Weight(g2) = 1
    c: Equal(g2,g3)
    c: Equal(g2,g4)
    c: Coincident(g5,g0)
    c: InternalAlignment(g2,g5)
    c: InternalAlignment(g3,g5)
    c: InternalAlignment(g4,g5)
    c: InternalAlignment(g6,g5)
    c: InternalAlignment(g7,g5)
    c: Block(g5)
    c: Vertical(g9)
    c: Coincident(g8,g9)
    c: Block(g9)
    c: Block(g8)
    c: Coincident(g10,g8)
    c: Coincident(g10,g1)
    c: Horizontal(g10)
    c: PointOnObject(g12,g-1)
    c: PointOnObject(g11,g-1)
    c: Block(g11)
    c: Block(g12)
    c: Coincident(g17,g9)
    c: Weight(g13) = 1
    c: Equal(g13,g14)
    c: Equal(g13,g15)
    c: Equal(g13,g16)
    c: Coincident(g17,g0)
    c: InternalAlignment(g13-g16 -> g17) x4
    c: InternalAlignment(g18,g17)
    c: InternalAlignment(g19,g17)
    c: Block(g17)
FEATURE [Part::Extrusion] Extrude007  label="attatchmentPieceBottom003"
  Base = -> Sketch006
  Dir = (0,0,1)
  DirMode = 2
  FaceMakerClass = Part::FaceMakerBullseye
  LengthFwd = 3.2
  LengthRev = 0
  Placement = pos=(0,0,-6.5) rot=(0,0,1;0rad)
  Solid = true
  Symmetric = false
FEATURE [Part::Cut] Cut003  label="mainBumpperPieceAttatchment004"
  Base = -> Fillet006
  Tool = -> Extrude005
FEATURE [Part::Chamfer] Chamfer
  Base = -> Extrude007
  Edges = 2 edges r=2.4: [Edge23,Edge26]
FEATURE [Part::Chamfer] Chamfer001  label="attatchmentPieceBottom004"
  Base = -> Chamfer
  Edges = 7 edges r=2.4: [Edge14,Edge15,Edge16,Edge17,Edge18,Edge19,Edge20]
FEATURE [Part::Fillet] Fillet007  label="attatchmentPieceBottom005"
  Base = -> Chamfer001
  Edges = 7 edges r=1.2: [Edge1,Edge2,Edge3,Edge4,Edge5,Edge6,Edge7]
FEATURE [Part::MultiFuse] Fusion007  label="attatchment"
  Shapes = -> [Fillet007,Fillet004,Fillet003,Fusion002,Extrude]
FEATURE [Part::Cylinder] Cylinder004  label="brace"
  Angle = 360
  AttacherType = Attacher::AttachEngine3D
  FirstAngle = 0
  Height = 32
  Placement = pos=(-42,0,0) rot=(0,1,0;1.5708rad)
  Radius = 2.4
  SecondAngle = 0
FEATURE [Part::Cylinder] Cylinder005  label="brace001"
  Angle = 360
  AttacherType = Attacher::AttachEngine3D
  FirstAngle = 0
  Height = 10
  Placement = pos=(29,0,0) rot=(0,1,0;1.5708rad)
  Radius = 2
  SecondAngle = 0
FEATURE [Part::Cylinder] Cylinder006  label="brace002"
  Angle = 360
  AttacherType = Attacher::AttachEngine3D
  FirstAngle = 0
  Height = 10
  Placement = pos=(-42,0,0) rot=(0,1,0;1.5708rad)
  Radius = 2
  SecondAngle = 0
FEATURE [Part::MultiFuse] Fusion008  label="leftBrace"
  Placement = pos=(-23,1.4,8) rot=(0,0,1;-0.785398rad)
  Shapes = -> [Cylinder004,Cylinder006]
FEATURE [Part::Cylinder] Cylinder007  label="brace003"
  Angle = 360
  AttacherType = Attacher::AttachEngine3D
  FirstAngle = 0
  Height = 32
  Placement = pos=(29,0,0) rot=(0,1,0;1.5708rad)
  Radius = 2.4
  SecondAngle = 0
FEATURE [Part::MultiFuse] Fusion009  label="rightBrace"
  Placement = pos=(6.4,-12,7) rot=(0,0,1;0.785398rad)
  Shapes = -> [Cylinder007,Cylinder005]
FEATURE [Part::Box] Box005  label="removeFromMainRight"
  AttacherType = Attacher::AttachEngine3D
  Height = 40
  Length = 44
  Placement = pos=(66,47,-6) rot=(0,0,1;-0.349066rad)
  Width = 20
FEATURE [Part::Box] Box006  label="removeFromMainLeft"
  AttacherType = Attacher::AttachEngine3D
  Height = 40
  Length = 44
  Placement = pos=(-110.35,31.95,-6) rot=(0,0,1;0.349066rad)
  Width = 20
FEATURE [Part::Cylinder] Cylinder008  label="brace004"
  Angle = 360
  AttacherType = Attacher::AttachEngine3D
  FirstAngle = 0
  Height = 32
  Placement = pos=(-42,0,0) rot=(0,1,0;1.5708rad)
  Radius = 2.4
  SecondAngle = 0
FEATURE [Part::Cylinder] Cylinder009  label="brace005"
  Angle = 360
  AttacherType = Attacher::AttachEngine3D
  FirstAngle = 0
  Height = 10
  Placement = pos=(-42,0,0) rot=(0,1,0;1.5708rad)
  Radius = 2
  SecondAngle = 0
FEATURE [Part::MultiFuse] Fusion010  label="leftBrace001"
  Placement = pos=(-23,1.4,-1) rot=(0,0,-1;0.785398rad)
  Shapes = -> [Cylinder008,Cylinder009]
FEATURE [Part::Cylinder] Cylinder010  label="brace006"
  Angle = 360
  AttacherType = Attacher::AttachEngine3D
  FirstAngle = 0
  Height = 10
  Placement = pos=(29,0,0) rot=(0,1,0;1.5708rad)
  Radius = 2
  SecondAngle = 0
FEATURE [Part::Cylinder] Cylinder011  label="brace007"
  Angle = 360
  AttacherType = Attacher::AttachEngine3D
  FirstAngle = 0
  Height = 32
  Placement = pos=(29,0,0) rot=(0,1,0;1.5708rad)
  Radius = 2.4
  SecondAngle = 0
FEATURE [Part::MultiFuse] Fusion011  label="rightBrace001"
  Placement = pos=(6.4,-12,-1) rot=(0,0,1;0.785398rad)
  Shapes = -> [Cylinder011,Cylinder010]
FEATURE [Part::Cylinder] Cylinder012  label="brace008"
  Angle = 360
  AttacherType = Attacher::AttachEngine3D
  FirstAngle = 0
  Height = 32
  Placement = pos=(-42,0,0) rot=(0,1,0;1.5708rad)
  Radius = 2.4
  SecondAngle = 0
FEATURE [Part::Cylinder] Cylinder013  label="brace009"
  Angle = 360
  AttacherType = Attacher::AttachEngine3D
  FirstAngle = 0
  Height = 10
  Placement = pos=(-42,0,0) rot=(0,1,0;1.5708rad)
  Radius = 2
  SecondAngle = 0
FEATURE [Part::MultiFuse] Fusion012  label="leftBrace002"
  Placement = pos=(-23,1.4,6) rot=(0,0,-1;0.785398rad)
  Shapes = -> [Cylinder012,Cylinder013]
FEATURE [Part::Cylinder] Cylinder014  label="brace010"
  Angle = 360
  AttacherType = Attacher::AttachEngine3D
  FirstAngle = 0
  Height = 10
  Placement = pos=(29,0,0) rot=(0,1,0;1.5708rad)
  Radius = 2
  SecondAngle = 0
FEATURE [Part::Cylinder] Cylinder015  label="brace011"
  Angle = 360
  AttacherType = Attacher::AttachEngine3D
  FirstAngle = 0
  Height = 32
  Placement = pos=(29,0,0) rot=(0,1,0;1.5708rad)
  Radius = 2.4
  SecondAngle = 0
FEATURE [Part::MultiFuse] Fusion013  label="rightBrace002"
  Placement = pos=(6.4,-12,5) rot=(0,0,1;0.785398rad)
  Shapes = -> [Cylinder015,Cylinder014]
FEATURE [Part::Cylinder] Cylinder016  label="brace012"
  Angle = 360
  AttacherType = Attacher::AttachEngine3D
  FirstAngle = 0
  Height = 10
  Placement = pos=(29,0,0) rot=(0,1,0;1.5708rad)
  Radius = 2
  SecondAngle = 0
FEATURE [Part::Cylinder] Cylinder017  label="brace013"
  Angle = 360
  AttacherType = Attacher::AttachEngine3D
  FirstAngle = 0
  Height = 32
  Placement = pos=(29,0,0) rot=(0,1,0;1.5708rad)
  Radius = 2.4
  SecondAngle = 0
FEATURE [Part::MultiFuse] Fusion014  label="rightBrace003"
  Placement = pos=(6.4,-12,2) rot=(0,0,1;0.785398rad)
  Shapes = -> [Cylinder017,Cylinder016]
FEATURE [Part::Cylinder] Cylinder018  label="brace014"
  Angle = 360
  AttacherType = Attacher::AttachEngine3D
  FirstAngle = 0
  Height = 32
  Placement = pos=(-42,0,0) rot=(0,1,0;1.5708rad)
  Radius = 2.4
  SecondAngle = 0
FEATURE [Part::Cylinder] Cylinder019  label="brace015"
  Angle = 360
  AttacherType = Attacher::AttachEngine3D
  FirstAngle = 0
  Height = 10
  Placement = pos=(-42,0,0) rot=(0,1,0;1.5708rad)
  Radius = 2
  SecondAngle = 0
FEATURE [Part::MultiFuse] Fusion015  label="leftBrace003"
  Placement = pos=(-23,1.4,2) rot=(0,0,-1;0.785398rad)
  Shapes = -> [Cylinder018,Cylinder019]
FEATURE [Part::Cut] Cut004
  Base = -> Extrude004
  Tool = -> Fusion001
FEATURE [Part::Cut] Cut005
  Base = -> Cut004
  Tool = -> Box006
FEATURE [Part::Cut] Cut006  label="main"
  Base = -> Cut005
  Tool = -> Box005
FEATURE [Part::Cylinder] Cylinder020  label="removeFromMain"
  Angle = 360
  AttacherType = Attacher::AttachEngine3D
  FirstAngle = 0
  Height = 40
  Placement = pos=(-1.5,39,-10) rot=(0,0,1;0rad)
  Radius = 4
  SecondAngle = 0
FEATURE [Part::Cylinder] Cylinder021  label="removeFromMain001"
  Angle = 360
  AttacherType = Attacher::AttachEngine3D
  FirstAngle = 0
  Height = 40
  Placement = pos=(-12.5,39,-10) rot=(0,0,1;0rad)
  Radius = 4
  SecondAngle = 0
FEATURE [Part::Cylinder] Cylinder022  label="removeFromMain002"
  Angle = 360
  AttacherType = Attacher::AttachEngine3D
  FirstAngle = 0
  Height = 40
  Placement = pos=(9.5,39,-10) rot=(0,0,1;0rad)
  Radius = 4
  SecondAngle = 0
FEATURE [Part::Cylinder] Cylinder023  label="removeFromMain003"
  Angle = 360
  AttacherType = Attacher::AttachEngine3D
  FirstAngle = 0
  Height = 40
  Placement = pos=(-34.5,39,-10) rot=(0,0,1;0rad)
  Radius = 4
  SecondAngle = 0
FEATURE [Part::Cylinder] Cylinder024  label="removeFromMain004"
  Angle = 360
  AttacherType = Attacher::AttachEngine3D
  FirstAngle = 0
  Height = 40
  Placement = pos=(31.5,39,-10) rot=(0,0,1;0rad)
  Radius = 4
  SecondAngle = 0
FEATURE [Part::Cylinder] Cylinder025  label="removeFromMain005"
  Angle = 360
  AttacherType = Attacher::AttachEngine3D
  FirstAngle = 0
  Height = 40
  Placement = pos=(-63.5,39,-10) rot=(0,0,1;0rad)
  Radius = 4
  SecondAngle = 0
FEATURE [Part::Cylinder] Cylinder026  label="removeFromMain006"
  Angle = 360
  AttacherType = Attacher::AttachEngine3D
  FirstAngle = 0
  Height = 40
  Placement = pos=(60.5,39,-10) rot=(0,0,1;0rad)
  Radius = 4
  SecondAngle = 0
FEATURE [Part::Cylinder] Cylinder027  label="removeFromMain007"
  Angle = 360
  AttacherType = Attacher::AttachEngine3D
  FirstAngle = 0
  Height = 40
  Placement = pos=(-74.5,38,-10) rot=(0,0,1;0rad)
  Radius = 4
  SecondAngle = 0
FEATURE [Part::Cylinder] Cylinder028  label="removeFromMain008"
  Angle = 360
  AttacherType = Attacher::AttachEngine3D
  FirstAngle = 0
  Height = 40
  Placement = pos=(71.5,38,-10) rot=(0,0,1;0rad)
  Radius = 4
  SecondAngle = 0
